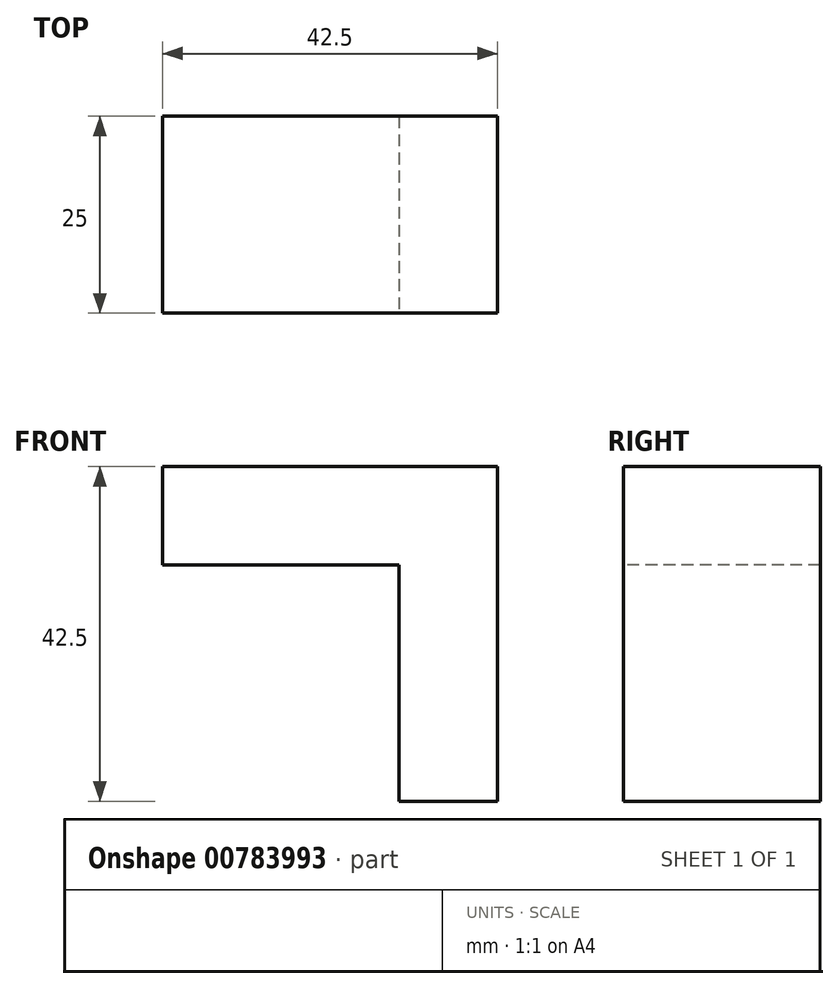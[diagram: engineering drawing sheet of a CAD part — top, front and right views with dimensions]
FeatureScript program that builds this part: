
annotation { "Feature Type Name" : "Feature", "Feature Type Description" : "" }
export const myFeature = defineFeature(function(context is Context, id is Id, definition is map)
    precondition{}
    {
        {
            var Q0;
            Q0=qCreatedBy(makeId("Front.planeOp"),FACE);
            var sketch = newSketch(context, id + "F0", { "sketchPlane" : qUnion([Q0])});
            skLineSegment(sketch, "E0", {"start": v(0, 0) * mm, "end": v(0, -30) * mm});
            skLineSegment(sketch, "E1", {"start": v(0, -30) * mm, "end": v(12.5, -30) * mm});
            skLineSegment(sketch, "E2", {"start": v(12.5, -30) * mm, "end": v(12.5, 12.5) * mm});
            skLineSegment(sketch, "E3", {"start": v(12.5, 12.5) * mm, "end": v(-30, 12.5) * mm});
            skLineSegment(sketch, "E4", {"start": v(-30, 12.5) * mm, "end": v(-30, 0) * mm});
            skLineSegment(sketch, "E5", {"start": v(-30, 0) * mm, "end": v(0, 0) * mm});
            skSolve(sketch);
        }
        {
            var Q0;
            Q0=makeQuery(id+"F0.imprint","IMPRINT",FACE,{"disambiguationData":[TD([[makeQuery(id+"F0.imprint","IMPRINT",EDGE,{"derivedFrom":sQuery(id+"F0.wireOp",EDGE,"E0")}),1.0]])]});
            extrude(context, id + "F1", {"entities" : qUnion([Q0]), "endBound" : BoundingType.SYMMETRIC, "oppositeDirection" : true, "depth" : 25 * mm, "offsetDistance" : 25 * mm});
        }
    });
